# Revit family: Haworth_CabanaLounge_Shelf
name_source: partatom
category: Furniture Systems
revit_build: Autodesk Revit 2018 (Build: 20170223_1515(x64)
units: mm (PartAtom-declared; Revit-internal decimal feet)

## family parameters
Always vertical = No
Cut with Voids When Loaded = No
OmniClass Number = 23.40.70.14.64.21
OmniClass Title = Systems Furniture
Part Type = Normal
Room Calculation Point = No
Round Connector Dimension = Use Diameter
Shared = No
Work Plane-Based = No

## types (4) — shared parameters
Actual Depth = 7"
Actual Height = 23"
Actual Width = 18"
Assembly Code = E2020200
Interior Finish = Haworth _ Grey _ Interior
Manufacturer = Haworth
Metal Finish = Haworth _ Metal _ Chrome
Model = S9SL
Revision Number = 1
Size = Verify Final Dimensions w/ Haworth
Sustainability Info = http://www.haworth.com
URL = www.haworth.com
URL - Product = https://www.haworth.com
Warranty = http://www.haworth.com
Width = 9 1/2"
Width Position = 4 3/4"

## per-type parameters (varying)
| type | Description | Lamp Control | Large | Medium | Small | With Lamp |
| S9SL - Shelf | Haworth - Cabana - Shelf | No | No | No | No | No |
| S9SL - Shelf - With Small Lana Light | Haworth - Cabana - Shelf - With Small Lana Light | Yes | No | No | Yes | Yes |
| S9SL - Shelf - With Medium Lana Light | Haworth - Cabana - Shelf - With Medium Lana Light | Yes | No | Yes | No | Yes |
| S9SL - Shelf - With Large Lana Light | Haworth - Cabana - Shelf - With Large Lana Light | Yes | Yes | No | No | Yes |

## geometry (parser evidence)
native form markers: Sweep x6
no freeform markers — native parametric forms only
